# Revit family: Camera-Canon-CR_X300
name_source: partatom
category: Communication Devices
units: mm (PartAtom-declared; Revit-internal decimal feet)

## family parameters
Cut with Voids When Loaded = No
Host = Face
Maintain Annotation Orientation = No
OmniClass Number = 23.85.10.14.11.14
OmniClass Title = Digital Cameras
Part Type = Normal
Room Calculation Point = No
Round Connector Dimension = Use Diameter
Shared = No

## types (1)
- CR-X300
    Amperage = 3.142 A
    Apparent Load = 38 VA
    Aspect Ratio = SDI: 1920 x 1080, 1280 x 720 | HDMI: 3840 x 2160, 1920 x 1080, 1280 x 720 | IP: 3840 x 2160, 1920 x 1080, 1280 x 720, 640 x 360 | USB: 1920 x 1080, 1280 x 720, 640 x 360
    Assembly Code = D5030900
    Constraints = 1
    Default Elevation = 0 "
    Depth = 8.54 "
    Description = The CR-X300 features a  1 / 2.3-inch 4k-UHD CMOS imaging sensor and an optical 20x zoom lens, along with the a 20x digital zoom, all supported by Canon’s highly advanced autofocus technology.
    Finish = Plastic - Canon - White
    Height = 12.24 "
    Housing = Plastic construction
    Instruction Sheet Link = https://www.usa.canon.com
    Keynote = 11 52 00
    Lens = f=3.67 – 73.4 mm, F/1.8 – 2.8, 20x optical zoom 35mm equivalent focal length
    Lens Finish = Screen - Canon - Black
    Manufacturer = Canon U.S.A., Inc.
    Material = Plastic Housing
    Model = CR-X300
    Mount Finish = <By Category>
    Number of Poles = 1
    Operating Humidity = 10% – 90% (without condensation)
    Operating Temperature = 32°F to 104°F (0°C to 40°C)
    Power Factor = 1
    Product Documentation Link = https://gdlp01.c-wss.com
    Product Name = PTZ & Remote Camera
    Product Page URL = https://www.usa.canon.com
    Trim Finish = Plastic - Canon - Black
    URL = https://www.usa.canon.com
    Version = 2020 - v1.0a
    Voltage = 12 V
    Voltage Notes = PoE: PoE++ power supply via LAN connector (IEEE802.3bt compliant) – PoE and PoE+ cannot be used | External power source: 12V DC
    Wattage = 38 W
    Wattage Notes = PoE++ Input: Approx. 39.8W* max. (body only) | DC Input: Approx. 37.7W max. (body only)
    Weight = 15.50 lbf
    Width = 8.54 "

## geometry (parser evidence)
native form markers: Sweep x20
no freeform markers — native parametric forms only
